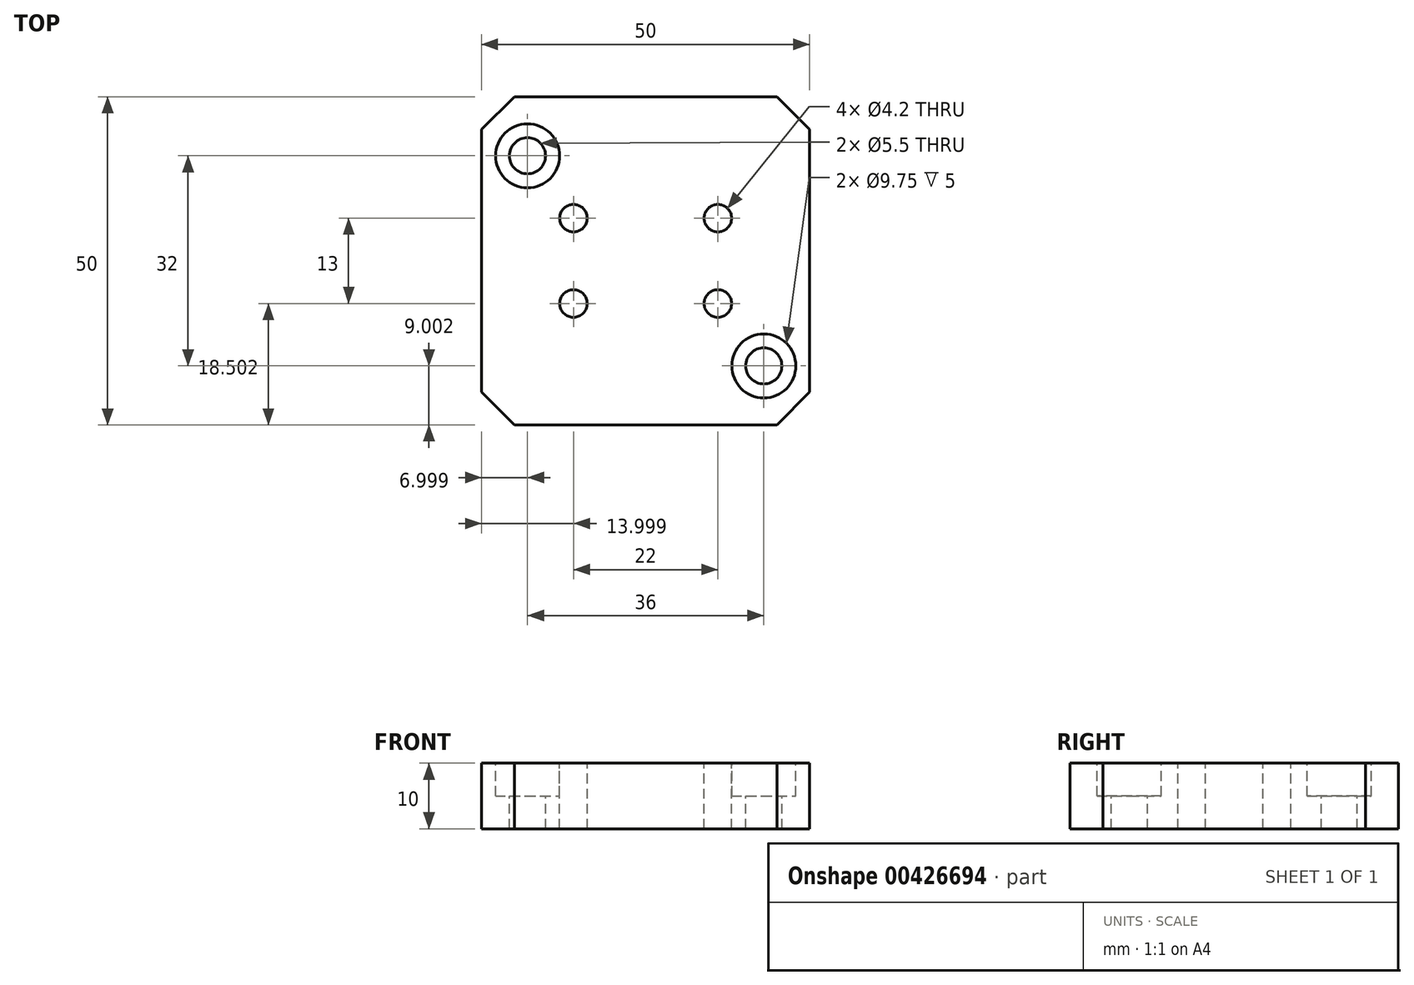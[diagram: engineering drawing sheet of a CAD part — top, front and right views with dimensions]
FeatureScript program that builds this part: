
annotation { "Feature Type Name" : "Feature", "Feature Type Description" : "" }
export const myFeature = defineFeature(function(context is Context, id is Id, definition is map)
    precondition{}
    {
        {
            var Q0;
            Q0=qCreatedBy(makeId("Top.planeOp"),FACE);
            var sketch = newSketch(context, id + "F0", { "sketchPlane" : qUnion([Q0])});
            skLineSegment(sketch, "E0.bottom", {"start": v(-0.53, 8.68) * mm, "end": v(49.47, 8.68) * mm});
            skLineSegment(sketch, "E0.top", {"start": v(-0.53, -41.32) * mm, "end": v(49.47, -41.32) * mm});
            skLineSegment(sketch, "E0.left", {"start": v(-0.53, 8.68) * mm, "end": v(-0.53, -41.32) * mm});
            skLineSegment(sketch, "E0.right", {"start": v(49.47, 8.68) * mm, "end": v(49.47, -41.32) * mm});
            skLineSegment(sketch, "E1.0", {"start": v(13.47, 8.68) * mm, "end": v(13.47, -41.32) * mm});
            skLineSegment(sketch, "E2.0", {"start": v(35.47, 8.68) * mm, "end": v(35.47, -41.32) * mm});
            skLineSegment(sketch, "E3.0", {"start": v(-0.53, -9.82) * mm, "end": v(49.47, -9.82) * mm});
            skLineSegment(sketch, "E4.0", {"start": v(-0.53, -22.82) * mm, "end": v(49.47, -22.82) * mm});
            skPoint(sketch, "E5", {"position": v(13.47, -9.82) * mm});
            skPoint(sketch, "E6", {"position": v(35.47, -9.82) * mm});
            skPoint(sketch, "E7", {"position": v(35.47, -22.82) * mm});
            skPoint(sketch, "E8", {"position": v(13.47, -22.82) * mm});
            skLineSegment(sketch, "E9.0", {"start": v(-0.53, -0.32) * mm, "end": v(49.47, -0.32) * mm});
            skLineSegment(sketch, "E10.0", {"start": v(-0.53, -32.32) * mm, "end": v(49.47, -32.32) * mm});
            skLineSegment(sketch, "E11.0", {"start": v(6.47, 8.68) * mm, "end": v(6.47, -41.32) * mm});
            skLineSegment(sketch, "E12.0", {"start": v(42.47, 8.68) * mm, "end": v(42.47, -41.32) * mm});
            skPoint(sketch, "E13", {"position": v(6.47, -0.32) * mm});
            skPoint(sketch, "E14", {"position": v(42.47, -0.32) * mm});
            skPoint(sketch, "E15", {"position": v(6.47, -32.32) * mm});
            skPoint(sketch, "E16", {"position": v(42.47, -32.32) * mm});
            skSolve(sketch);
        }
        {
            var Q0;
            {var subQ0=sQuery(id+"F0.wireOp",EDGE,"E0.right");var subQ1=sQuery(id+"F0.wireOp",EDGE,"E0.top");var subQ2=makeQuery(id+"F0.imprint","INTERSECT",VERTEX,{"derivedFrom":[subQ1,subQ0]});Q0=makeQuery(id+"F0.imprint","IMPRINT",FACE,{"disambiguationData":[TD([[makeQuery(id+"F0.imprint","IMPRINT",EDGE,{"disambiguationData":[TD([[subQ2,1.0]])],"derivedFrom":subQ1}),1.0]])]});}
            var Q1;
            {var subQ0=sQuery(id+"F0.wireOp",EDGE,"E3.0");var subQ1=sQuery(id+"F0.wireOp",EDGE,"E0.right");var subQ2=makeQuery(id+"F0.imprint","INTERSECT",VERTEX,{"derivedFrom":[subQ1,subQ0]});Q1=makeQuery(id+"F0.imprint","IMPRINT",FACE,{"disambiguationData":[TD([[makeQuery(id+"F0.imprint","IMPRINT",EDGE,{"disambiguationData":[TD([[subQ2,-1.0]])],"derivedFrom":subQ1}),-1.0]])]});}
            var Q2;
            {var subQ0=sQuery(id+"F0.wireOp",EDGE,"E0.right");var subQ1=sQuery(id+"F0.wireOp",EDGE,"E0.bottom");var subQ2=makeQuery(id+"F0.imprint","INTERSECT",VERTEX,{"derivedFrom":[subQ1,subQ0]});Q2=makeQuery(id+"F0.imprint","IMPRINT",FACE,{"disambiguationData":[TD([[makeQuery(id+"F0.imprint","IMPRINT",EDGE,{"disambiguationData":[TD([[subQ2,1.0]])],"derivedFrom":subQ1}),-1.0]])]});}
            var Q3;
            {var subQ0=sQuery(id+"F0.wireOp",EDGE,"E1.0");var subQ1=sQuery(id+"F0.wireOp",EDGE,"E0.bottom");var subQ2=makeQuery(id+"F0.imprint","INTERSECT",VERTEX,{"derivedFrom":[subQ1,subQ0]});Q3=makeQuery(id+"F0.imprint","IMPRINT",FACE,{"disambiguationData":[TD([[makeQuery(id+"F0.imprint","IMPRINT",EDGE,{"disambiguationData":[TD([[subQ2,-1.0]])],"derivedFrom":subQ1}),-1.0]])]});}
            var Q4;
            {var subQ0=sQuery(id+"F0.wireOp",EDGE,"E0.left");var subQ1=sQuery(id+"F0.wireOp",EDGE,"E0.bottom");var subQ2=makeQuery(id+"F0.imprint","INTERSECT",VERTEX,{"derivedFrom":[subQ1,subQ0]});Q4=makeQuery(id+"F0.imprint","IMPRINT",FACE,{"disambiguationData":[TD([[makeQuery(id+"F0.imprint","IMPRINT",EDGE,{"disambiguationData":[TD([[subQ2,-1.0]])],"derivedFrom":subQ1}),-1.0]])]});}
            var Q5;
            {var subQ0=sQuery(id+"F0.wireOp",EDGE,"E3.0");var subQ1=sQuery(id+"F0.wireOp",EDGE,"E0.left");var subQ2=makeQuery(id+"F0.imprint","INTERSECT",VERTEX,{"derivedFrom":[subQ1,subQ0]});Q5=makeQuery(id+"F0.imprint","IMPRINT",FACE,{"disambiguationData":[TD([[makeQuery(id+"F0.imprint","IMPRINT",EDGE,{"disambiguationData":[TD([[subQ2,-1.0]])],"derivedFrom":subQ1}),1.0]])]});}
            var Q6;
            {var subQ0=sQuery(id+"F0.wireOp",EDGE,"E3.0");var subQ1=sQuery(id+"F0.wireOp",EDGE,"E1.0");var subQ2=makeQuery(id+"F0.imprint","INTERSECT",VERTEX,{"derivedFrom":[subQ1,subQ0]});Q6=makeQuery(id+"F0.imprint","IMPRINT",FACE,{"disambiguationData":[TD([[makeQuery(id+"F0.imprint","IMPRINT",EDGE,{"disambiguationData":[TD([[subQ2,-1.0]])],"derivedFrom":subQ1}),1.0]])]});}
            var Q7;
            {var subQ0=sQuery(id+"F0.wireOp",EDGE,"E1.0");var subQ1=sQuery(id+"F0.wireOp",EDGE,"E0.top");var subQ2=makeQuery(id+"F0.imprint","INTERSECT",VERTEX,{"derivedFrom":[subQ1,subQ0]});Q7=makeQuery(id+"F0.imprint","IMPRINT",FACE,{"disambiguationData":[TD([[makeQuery(id+"F0.imprint","IMPRINT",EDGE,{"disambiguationData":[TD([[subQ2,-1.0]])],"derivedFrom":subQ1}),1.0]])]});}
            var Q8;
            {var subQ0=sQuery(id+"F0.wireOp",EDGE,"E0.left");var subQ1=sQuery(id+"F0.wireOp",EDGE,"E0.top");var subQ2=makeQuery(id+"F0.imprint","INTERSECT",VERTEX,{"derivedFrom":[subQ1,subQ0]});Q8=makeQuery(id+"F0.imprint","IMPRINT",FACE,{"disambiguationData":[TD([[makeQuery(id+"F0.imprint","IMPRINT",EDGE,{"disambiguationData":[TD([[subQ2,-1.0]])],"derivedFrom":subQ1}),1.0]])]});}
            var Q9;
            {var subQ0=sQuery(id+"F0.wireOp",EDGE,"E3.0");var subQ1=sQuery(id+"F0.wireOp",EDGE,"E0.left");var subQ2=makeQuery(id+"F0.imprint","INTERSECT",VERTEX,{"derivedFrom":[subQ1,subQ0]});Q9=makeQuery(id+"F0.imprint","IMPRINT",FACE,{"disambiguationData":[TD([[makeQuery(id+"F0.imprint","IMPRINT",EDGE,{"disambiguationData":[TD([[subQ2,1.0]])],"derivedFrom":subQ1}),1.0]])]});}
            var Q10;
            {var subQ0=sQuery(id+"F0.wireOp",EDGE,"E9.0");var subQ1=sQuery(id+"F0.wireOp",EDGE,"E1.0");var subQ2=makeQuery(id+"F0.imprint","INTERSECT",VERTEX,{"derivedFrom":[subQ1,subQ0]});Q10=makeQuery(id+"F0.imprint","IMPRINT",FACE,{"disambiguationData":[TD([[makeQuery(id+"F0.imprint","IMPRINT",EDGE,{"disambiguationData":[TD([[subQ2,-1.0]])],"derivedFrom":subQ1}),-1.0]])]});}
            var Q11;
            {var subQ0=sQuery(id+"F0.wireOp",EDGE,"E1.0");var subQ1=sQuery(id+"F0.wireOp",EDGE,"E0.bottom");var subQ2=makeQuery(id+"F0.imprint","INTERSECT",VERTEX,{"derivedFrom":[subQ1,subQ0]});Q11=makeQuery(id+"F0.imprint","IMPRINT",FACE,{"disambiguationData":[TD([[makeQuery(id+"F0.imprint","IMPRINT",EDGE,{"disambiguationData":[TD([[subQ2,1.0]])],"derivedFrom":subQ1}),-1.0]])]});}
            var Q12;
            {var subQ0=sQuery(id+"F0.wireOp",EDGE,"E9.0");var subQ1=sQuery(id+"F0.wireOp",EDGE,"E1.0");var subQ2=makeQuery(id+"F0.imprint","INTERSECT",VERTEX,{"derivedFrom":[subQ1,subQ0]});Q12=makeQuery(id+"F0.imprint","IMPRINT",FACE,{"disambiguationData":[TD([[makeQuery(id+"F0.imprint","IMPRINT",EDGE,{"disambiguationData":[TD([[subQ2,-1.0]])],"derivedFrom":subQ1}),1.0]])]});}
            var Q13;
            {var subQ0=sQuery(id+"F0.wireOp",EDGE,"E9.0");var subQ1=sQuery(id+"F0.wireOp",EDGE,"E2.0");var subQ2=makeQuery(id+"F0.imprint","INTERSECT",VERTEX,{"derivedFrom":[subQ1,subQ0]});Q13=makeQuery(id+"F0.imprint","IMPRINT",FACE,{"disambiguationData":[TD([[makeQuery(id+"F0.imprint","IMPRINT",EDGE,{"disambiguationData":[TD([[subQ2,-1.0]])],"derivedFrom":subQ1}),1.0]])]});}
            var Q14;
            {var subQ0=sQuery(id+"F0.wireOp",EDGE,"E2.0");var subQ1=sQuery(id+"F0.wireOp",EDGE,"E0.bottom");var subQ2=makeQuery(id+"F0.imprint","INTERSECT",VERTEX,{"derivedFrom":[subQ1,subQ0]});Q14=makeQuery(id+"F0.imprint","IMPRINT",FACE,{"disambiguationData":[TD([[makeQuery(id+"F0.imprint","IMPRINT",EDGE,{"disambiguationData":[TD([[subQ2,-1.0]])],"derivedFrom":subQ1}),-1.0]])]});}
            var Q15;
            {var subQ0=sQuery(id+"F0.wireOp",EDGE,"E3.0");var subQ1=sQuery(id+"F0.wireOp",EDGE,"E0.right");var subQ2=makeQuery(id+"F0.imprint","INTERSECT",VERTEX,{"derivedFrom":[subQ1,subQ0]});Q15=makeQuery(id+"F0.imprint","IMPRINT",FACE,{"disambiguationData":[TD([[makeQuery(id+"F0.imprint","IMPRINT",EDGE,{"disambiguationData":[TD([[subQ2,1.0]])],"derivedFrom":subQ1}),-1.0]])]});}
            var Q16;
            {var subQ0=sQuery(id+"F0.wireOp",EDGE,"E3.0");var subQ1=sQuery(id+"F0.wireOp",EDGE,"E2.0");var subQ2=makeQuery(id+"F0.imprint","INTERSECT",VERTEX,{"derivedFrom":[subQ1,subQ0]});Q16=makeQuery(id+"F0.imprint","IMPRINT",FACE,{"disambiguationData":[TD([[makeQuery(id+"F0.imprint","IMPRINT",EDGE,{"disambiguationData":[TD([[subQ2,-1.0]])],"derivedFrom":subQ1}),1.0]])]});}
            var Q17;
            {var subQ0=sQuery(id+"F0.wireOp",EDGE,"E3.0");var subQ1=sQuery(id+"F0.wireOp",EDGE,"E1.0");var subQ2=makeQuery(id+"F0.imprint","INTERSECT",VERTEX,{"derivedFrom":[subQ1,subQ0]});Q17=makeQuery(id+"F0.imprint","IMPRINT",FACE,{"disambiguationData":[TD([[makeQuery(id+"F0.imprint","IMPRINT",EDGE,{"disambiguationData":[TD([[subQ2,-1.0]])],"derivedFrom":subQ1}),-1.0]])]});}
            var Q18;
            {var subQ0=sQuery(id+"F0.wireOp",EDGE,"E4.0");var subQ1=sQuery(id+"F0.wireOp",EDGE,"E0.left");var subQ2=makeQuery(id+"F0.imprint","INTERSECT",VERTEX,{"derivedFrom":[subQ1,subQ0]});Q18=makeQuery(id+"F0.imprint","IMPRINT",FACE,{"disambiguationData":[TD([[makeQuery(id+"F0.imprint","IMPRINT",EDGE,{"disambiguationData":[TD([[subQ2,-1.0]])],"derivedFrom":subQ1}),1.0]])]});}
            var Q19;
            {var subQ0=sQuery(id+"F0.wireOp",EDGE,"E4.0");var subQ1=sQuery(id+"F0.wireOp",EDGE,"E1.0");var subQ2=makeQuery(id+"F0.imprint","INTERSECT",VERTEX,{"derivedFrom":[subQ1,subQ0]});Q19=makeQuery(id+"F0.imprint","IMPRINT",FACE,{"disambiguationData":[TD([[makeQuery(id+"F0.imprint","IMPRINT",EDGE,{"disambiguationData":[TD([[subQ2,-1.0]])],"derivedFrom":subQ1}),-1.0]])]});}
            var Q20;
            {var subQ0=sQuery(id+"F0.wireOp",EDGE,"E4.0");var subQ1=sQuery(id+"F0.wireOp",EDGE,"E1.0");var subQ2=makeQuery(id+"F0.imprint","INTERSECT",VERTEX,{"derivedFrom":[subQ1,subQ0]});Q20=makeQuery(id+"F0.imprint","IMPRINT",FACE,{"disambiguationData":[TD([[makeQuery(id+"F0.imprint","IMPRINT",EDGE,{"disambiguationData":[TD([[subQ2,-1.0]])],"derivedFrom":subQ1}),1.0]])]});}
            var Q21;
            {var subQ0=sQuery(id+"F0.wireOp",EDGE,"E4.0");var subQ1=sQuery(id+"F0.wireOp",EDGE,"E2.0");var subQ2=makeQuery(id+"F0.imprint","INTERSECT",VERTEX,{"derivedFrom":[subQ1,subQ0]});Q21=makeQuery(id+"F0.imprint","IMPRINT",FACE,{"disambiguationData":[TD([[makeQuery(id+"F0.imprint","IMPRINT",EDGE,{"disambiguationData":[TD([[subQ2,-1.0]])],"derivedFrom":subQ1}),1.0]])]});}
            var Q22;
            {var subQ0=sQuery(id+"F0.wireOp",EDGE,"E4.0");var subQ1=sQuery(id+"F0.wireOp",EDGE,"E0.right");var subQ2=makeQuery(id+"F0.imprint","INTERSECT",VERTEX,{"derivedFrom":[subQ1,subQ0]});Q22=makeQuery(id+"F0.imprint","IMPRINT",FACE,{"disambiguationData":[TD([[makeQuery(id+"F0.imprint","IMPRINT",EDGE,{"disambiguationData":[TD([[subQ2,-1.0]])],"derivedFrom":subQ1}),-1.0]])]});}
            var Q23;
            {var subQ0=sQuery(id+"F0.wireOp",EDGE,"E1.0");var subQ1=sQuery(id+"F0.wireOp",EDGE,"E0.top");var subQ2=makeQuery(id+"F0.imprint","INTERSECT",VERTEX,{"derivedFrom":[subQ1,subQ0]});Q23=makeQuery(id+"F0.imprint","IMPRINT",FACE,{"disambiguationData":[TD([[makeQuery(id+"F0.imprint","IMPRINT",EDGE,{"disambiguationData":[TD([[subQ2,1.0]])],"derivedFrom":subQ1}),1.0]])]});}
            var Q24;
            {var subQ0=sQuery(id+"F0.wireOp",EDGE,"E2.0");var subQ1=sQuery(id+"F0.wireOp",EDGE,"E0.top");var subQ2=makeQuery(id+"F0.imprint","INTERSECT",VERTEX,{"derivedFrom":[subQ1,subQ0]});Q24=makeQuery(id+"F0.imprint","IMPRINT",FACE,{"disambiguationData":[TD([[makeQuery(id+"F0.imprint","IMPRINT",EDGE,{"disambiguationData":[TD([[subQ2,-1.0]])],"derivedFrom":subQ1}),1.0]])]});}
            extrude(context, id + "F1", {"entities" : qUnion([Q0, Q1, Q2, Q3, Q4, Q5, Q6, Q7, Q8, Q9, Q10, Q11, Q12, Q13, Q14, Q15, Q16, Q17, Q18, Q19, Q20, Q21, Q22, Q23, Q24]), "depth" : 10 * mm});
        }
        {
            var Q0;
            Q0=sQuery(id+"F0.wireOp",VERTEX,"E5");
            var Q1;
            Q1=sQuery(id+"F0.wireOp",VERTEX,"E6");
            var Q2;
            Q2=sQuery(id+"F0.wireOp",VERTEX,"E7");
            var Q3;
            Q3=sQuery(id+"F0.wireOp",VERTEX,"E8");
            var Q4;
            Q4=makeQuery(id+"F1.opExtrude","SWEPT_BODY",BODY,{"disambiguationData":[OSD([sQuery(id+"F0.wireOp",EDGE,"E0.bottom"),sQuery(id+"F0.wireOp",EDGE,"E0.top"),sQuery(id+"F0.wireOp",EDGE,"E0.left"),sQuery(id+"F0.wireOp",EDGE,"E0.right")])]});
            hole(context, id + "F2", {"style" : HoleStyle.SIMPLE, "endStyle" : HoleEndStyle.THROUGH, "oppositeDirection" : true, "standardTappedOrClearance" : lookupTablePath({ "standard" : "ISO", "engagement" : "75%", "pitch" : "0.8 mm", "size" : "M5", "type" : "Tapped" }), "standardBlindInLast" : lookupTablePath({ "standard" : "ISO", "engagement" : "75%", "pitch" : "0.8 mm", "size" : "M5", "type" : "Tapped" }), "holeDiameter" : 4.2 * mm, "showTappedDepth" : true, "isTappedThrough" : true, "tappedDepth" : 10 * mm, "tapClearance" : 3, "locations" : qUnion([Q0, Q1, Q2, Q3]), "scope" : qUnion([Q4]), "majorDiameter" : 5 * mm});
        }
        {
            var Q0;
            Q0=makeQuery(id+"F1.opExtrude","SWEPT_EDGE",EDGE,{"disambiguationData":[OSD([sQuery(id+"F0.wireOp",EDGE,"E0.bottom"),sQuery(id+"F0.wireOp",EDGE,"E0.right")])]});
            var Q1;
            Q1=makeQuery(id+"F1.opExtrude","SWEPT_EDGE",EDGE,{"disambiguationData":[OSD([sQuery(id+"F0.wireOp",EDGE,"E0.top"),sQuery(id+"F0.wireOp",EDGE,"E0.right")])]});
            var Q2;
            Q2=makeQuery(id+"F1.opExtrude","SWEPT_EDGE",EDGE,{"disambiguationData":[OSD([sQuery(id+"F0.wireOp",EDGE,"E0.top"),sQuery(id+"F0.wireOp",EDGE,"E0.left")])]});
            var Q3;
            Q3=makeQuery(id+"F1.opExtrude","SWEPT_EDGE",EDGE,{"disambiguationData":[OSD([sQuery(id+"F0.wireOp",EDGE,"E0.bottom"),sQuery(id+"F0.wireOp",EDGE,"E0.left")])]});
            chamfer(context, id + "F3", {"entities" : qUnion([Q0, Q1, Q2, Q3]), "width" : 5 * mm, "tangentPropagation" : true});
        }
        {
            var Q0;
            Q0=sQuery(id+"F0.wireOp",VERTEX,"E13");
            var Q1;
            Q1=sQuery(id+"F0.wireOp",VERTEX,"E16");
            var Q2;
            Q2=makeQuery(id+"F1.opExtrude","SWEPT_BODY",BODY,{"disambiguationData":[OSD([sQuery(id+"F0.wireOp",EDGE,"E0.bottom"),sQuery(id+"F0.wireOp",EDGE,"E0.top"),sQuery(id+"F0.wireOp",EDGE,"E0.left"),sQuery(id+"F0.wireOp",EDGE,"E0.right")])]});
            hole(context, id + "F4", {"style" : HoleStyle.C_BORE, "endStyle" : HoleEndStyle.THROUGH, "oppositeDirection" : true, "standardTappedOrClearance" : lookupTablePath({ "standard" : "ISO", "fit" : "Normal", "size" : "M5", "type" : "Clearance" }), "standardBlindInLast" : lookupTablePath({ "fit" : "Standard", "standard" : "ISO", "size" : "M5", "type" : "Clearance" }), "holeDiameter" : 5.5 * mm, "cBoreDiameter" : 9.75 * mm, "cBoreDepth" : 5 * mm, "isTappedThrough" : true, "tappedDepth" : 10 * mm, "tapClearance" : 3, "locations" : qUnion([Q0, Q1]), "scope" : qUnion([Q2])});
        }
        {
            var Q0;
            Q0=makeQuery(id+"F1.opExtrude","SWEPT_BODY",BODY,{"disambiguationData":[OSD([sQuery(id+"F0.wireOp",EDGE,"E0.bottom"),sQuery(id+"F0.wireOp",EDGE,"E0.top"),sQuery(id+"F0.wireOp",EDGE,"E0.left"),sQuery(id+"F0.wireOp",EDGE,"E0.right")])]});
            var Q1;
            Q1=qCreatedBy(makeId("Top.planeOp"),FACE);
            mirror(context, id + "F5", {"entities" : qUnion([Q0]), "mirrorPlane" : qUnion([Q1])});
        }
        {
            var Q0;
            Q0=makeQuery(id+"F1.opExtrude","SWEPT_BODY",BODY,{"disambiguationData":[OSD([sQuery(id+"F0.wireOp",EDGE,"E0.bottom"),sQuery(id+"F0.wireOp",EDGE,"E0.top"),sQuery(id+"F0.wireOp",EDGE,"E0.left"),sQuery(id+"F0.wireOp",EDGE,"E0.right")])]});
            deleteBodies(context, id + "F6", {"entities" : qUnion([Q0])});
        }
    });
